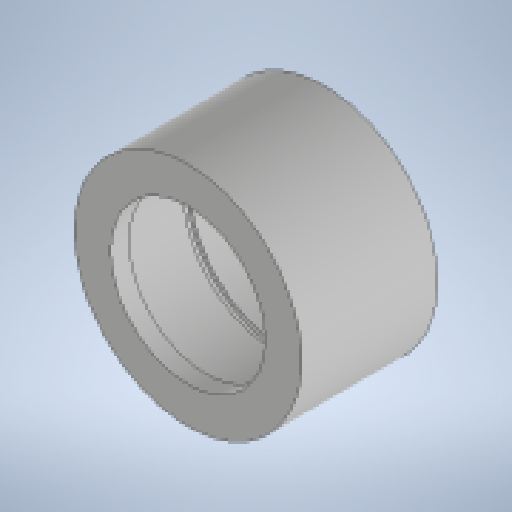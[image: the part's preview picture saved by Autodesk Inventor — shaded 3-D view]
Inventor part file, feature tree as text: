
AUTODESK INVENTOR PART (.ipt)
format: ipt  version: 2025 (Build 290162010, 162A)  size: 249,856 bytes
history: native  units: mm
features: revolve x1, sketch x1
ambient origin geometry x8: Origin, YZ Plane, XZ Plane, XY Plane, X Axis, Y Axis, Z Axis, Center Point
bodies: Body1 (feature_tree)
feature tree (2):
  revolve  "Revolution1"  [1 undecoded]
  sketch  "Sketch5"  dims[d12=30.0mm d13=4.0mm d14=3.0mm d15=25.0mm d16=5.0mm d17=1.6mm d19=15.0mm d20=1.0mm d21=1.0mm d22=1.6mm d23=7.0mm d24=14.0mm d25=360.0deg]
note: 1 required parameter value undecoded (feature->parameter linkage not recoverable at this tier; creation-order binding heuristic only, values carry confidence <= 0.55)
